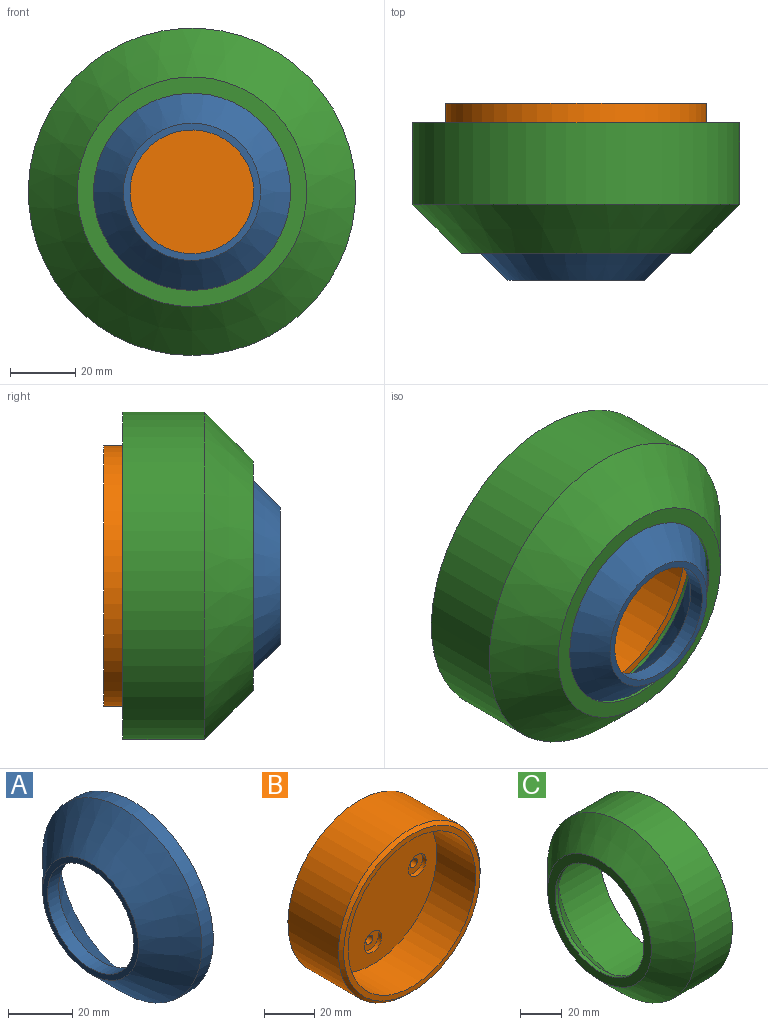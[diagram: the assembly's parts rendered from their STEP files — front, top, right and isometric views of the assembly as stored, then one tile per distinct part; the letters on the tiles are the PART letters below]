
ASSEMBLY  parts=3 mates=2
PART A: 6 faces, bbox 19x70x70 mm
  f0: cone r=33mm half-angle=45deg, axis (1,0,0), area 3234.4mm2, adj f1,f5
  f1: plane 70x70mm, normal (1,0,0), area 427.3mm2, adj f0,f2
  f2: cylinder r=35mm len=70mm, axis (-1,0,0), area 1115.2mm2, adj f1,f3
  f3: cone r=21.07mm half-angle=45deg, axis (1,0,0), area 3469.9mm2, adj f2,f4
  f4: plane 42.14x42.14mm, normal (-1,0,0), area 260.7mm2, adj f3,f5
  f5: cylinder r=19mm len=38mm, axis (-1,0,0), area 596.9mm2, adj f0,f4
PART B: 21 faces, bbox 80x30.6x80 mm
  f0: cylinder r=40mm len=80mm, axis (0,1,0), area 7162.8mm2, adj f2,f20
  f1: plane 77x77mm, normal (0,-1,0), area 585.1mm2, adj f7,f20
  f2: plane 80x80mm, normal (0,1,0), area 4881.2mm2, adj f0,f3,f8,f11,f14,f17
  f3: cylinder r=5.5mm len=11mm, axis (0,1,0), area 17.3mm2, adj f2,f5
  f4: plane 8x8mm, normal (0,1,0), area 50.3mm2, adj f5
  f5: torus R=4mm, axis (0,1,0), area 73.4mm2, adj f3,f4
  f6: plane 72x72mm, normal (0,-1,0), area 3757.3mm2, adj f7,f10,f13,f16,f19
  f7: cylinder r=36mm len=72mm, axis (0,-1,0), area 4976.3mm2, adj f1,f6
  f8: cylinder r=2mm len=6mm, axis (0,-1,0), area 75.4mm2, adj f2,f9
  f9: plane 10x10mm, normal (0,-1,0), area 66mm2, adj f8,f10
  f10: cylinder r=5mm len=10mm, axis (0,-1,0), area 62.8mm2, adj f6,f9
  f11: cylinder r=2mm len=6mm, axis (0,-1,0), area 75.4mm2, adj f2,f12
  f12: plane 10x10mm, normal (0,-1,0), area 66mm2, adj f11,f13
  f13: cylinder r=5mm len=10mm, axis (0,-1,0), area 62.8mm2, adj f6,f12
  f14: cylinder r=2mm len=6mm, axis (0,-1,0), area 75.4mm2, adj f2,f15
  f15: plane 10x10mm, normal (0,-1,0), area 66mm2, adj f14,f16
  f16: cylinder r=5mm len=10mm, axis (0,-1,0), area 62.8mm2, adj f6,f15
  f17: cylinder r=2mm len=6mm, axis (0,-1,0), area 75.4mm2, adj f2,f18
  f18: plane 10x10mm, normal (0,-1,0), area 66mm2, adj f17,f19
  f19: cylinder r=5mm len=10mm, axis (0,-1,0), area 62.8mm2, adj f6,f18
  f20: cone r=38.5mm half-angle=45deg, axis (0,1,0), area 523.1mm2, adj f0,f1
PART C: 7 faces, bbox 40.1x100.5x100.5 mm
  f0: cone r=30.25mm half-angle=45deg, axis (1,0,0), area 3132.2mm2, adj f1,f6
  f1: cylinder r=40.25mm len=80.5mm, axis (-1,0,0), area 7081.1mm2, adj f0,f2
  f2: plane 100.5x100.5mm, normal (1,0,0), area 2843.1mm2, adj f1,f3
  f3: cylinder r=50.25mm len=100.5mm, axis (-1,0,0), area 7915.7mm2, adj f2,f4
  f4: cone r=50.25mm half-angle=45deg, axis (1,0,0), area 5698mm2, adj f3,f5
  f5: plane 70.5x70.5mm, normal (-1,0,0), area 1028.9mm2, adj f4,f6
  f6: cylinder r=30.25mm len=60.5mm, axis (-1,0,0), area 393.6mm2, adj f0,f5
PLACE A rot(axis=(-0.58,-0.58,0.58),120deg) t=(0,-40.31,0)mm
PLACE B at identity fixed
PLACE C rot(axis=(0.71,0.71,0),180deg) t=(0,-30.95,0)mm
MATE slider A.f0 <-> B.f7  axis (0,-1,0) through (0,-37.78,0)mm
MATE slider C.f0 <-> B.f0  axis (0,-1,0) through (0,-19.88,0)mm
